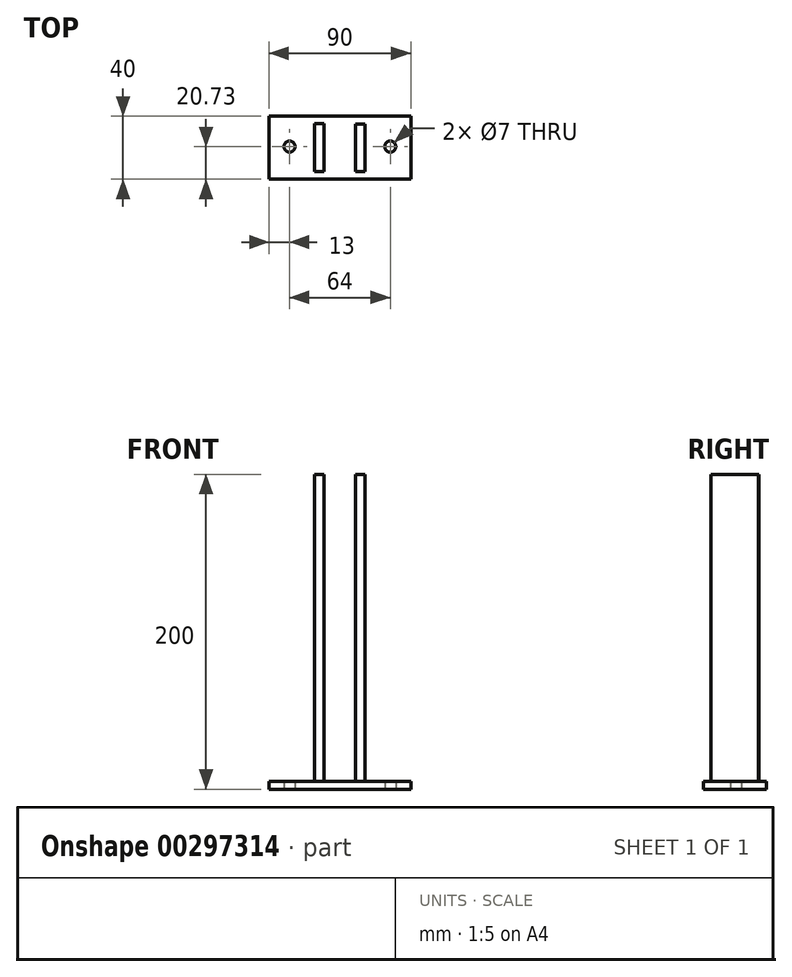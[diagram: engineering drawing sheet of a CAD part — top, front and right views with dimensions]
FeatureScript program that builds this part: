
annotation { "Feature Type Name" : "Feature", "Feature Type Description" : "" }
export const myFeature = defineFeature(function(context is Context, id is Id, definition is map)
    precondition{}
    {
        {
            var Q0;
            Q0=qCreatedBy(makeId("Right.planeOp"),FACE);
            var sketch = newSketch(context, id + "F0", { "sketchPlane" : qUnion([Q0])});
            skLineSegment(sketch, "E0.bottom", {"start": v(-20.73, 5) * mm, "end": v(19.27, 5) * mm});
            skLineSegment(sketch, "E0.left", {"start": v(-20.73, 5) * mm, "end": v(-20.73, 0) * mm});
            skLineSegment(sketch, "E0.right", {"start": v(19.27, 5) * mm, "end": v(19.27, 0) * mm});
            skLineSegment(sketch, "E1.trimOffspring", {"start": v(-20.73, 0) * mm, "end": v(19.27, 0) * mm});
            skSolve(sketch);
        }
        {
            var Q0;
            {var subQ3=sQuery(id+"F0.wireOp",EDGE,"ff7b447e-6627-4066-b775-27bb9192647b.left");Q0=makeQuery(id+"F0.imprint","IMPRINT",FACE,{"disambiguationData":[TD([[makeQuery(id+"F0.imprint","IMPRINT",EDGE,{"derivedFrom":subQ3}),-1.0]])]});}
            var Q1;
            {var subQ3=sQuery(id+"F0.wireOp",EDGE,"ff7b447e-6627-4066-b775-27bb9192647b.right");Q1=makeQuery(id+"F0.imprint","IMPRINT",FACE,{"disambiguationData":[TD([[makeQuery(id+"F0.imprint","IMPRINT",EDGE,{"derivedFrom":subQ3}),1.0]])]});}
            var Q2;
            {var subQ0=sQuery(id+"F0.wireOp",EDGE,"ff7b447e-6627-4066-b775-27bb9192647b.top");Q2=makeQuery(id+"F0.imprint","IMPRINT",FACE,{"disambiguationData":[TD([[makeQuery(id+"F0.imprint","IMPRINT",EDGE,{"derivedFrom":subQ0}),-1.0]])]});}
            var Q3;
            {var subQ5=sQuery(id+"F0.wireOp",EDGE,"E0.left");Q3=makeQuery(id+"F0.imprint","IMPRINT",FACE,{"disambiguationData":[TD([[makeQuery(id+"F0.imprint","IMPRINT",EDGE,{"derivedFrom":subQ5}),1.0]])]});}
            var Q4;
            {var subQ5=sQuery(id+"F0.wireOp",EDGE,"E0.right");Q4=makeQuery(id+"F0.imprint","IMPRINT",FACE,{"disambiguationData":[TD([[makeQuery(id+"F0.imprint","IMPRINT",EDGE,{"derivedFrom":subQ5}),-1.0]])]});}
            extrude(context, id + "F1", {"entities" : qUnion([Q0, Q1, Q2, Q3, Q4]), "depth" : 90 * mm});
        }
        {
            var Q0;
            Q0=qCreatedBy(makeId("Top.planeOp"),FACE);
            var sketch = newSketch(context, id + "F2", { "sketchPlane" : qUnion([Q0])});
            skLineSegment(sketch, "E2.bottom", {"start": v(29, 14.5) * mm, "end": v(35, 14.5) * mm});
            skLineSegment(sketch, "E2.top", {"start": v(29, -15.98) * mm, "end": v(35, -15.98) * mm});
            skLineSegment(sketch, "E2.left", {"start": v(29, 14.5) * mm, "end": v(29, -15.98) * mm});
            skLineSegment(sketch, "E2.right", {"start": v(35, 14.5) * mm, "end": v(35, -15.98) * mm});
            skLineSegment(sketch, "E3.bottom", {"start": v(55, 14.27) * mm, "end": v(61, 14.27) * mm});
            skLineSegment(sketch, "E3.top", {"start": v(55, -15.73) * mm, "end": v(61, -15.73) * mm});
            skLineSegment(sketch, "E3.left", {"start": v(55, 14.27) * mm, "end": v(55, -15.73) * mm});
            skLineSegment(sketch, "E3.right", {"start": v(61, 14.27) * mm, "end": v(61, -15.73) * mm});
            skLineSegment(sketch, "E4", {"start": v(0, -20.73) * mm, "end": v(90, -20.73) * mm, "construction": true});
            skLineSegment(sketch, "E5", {"start": v(90, 19.27) * mm, "end": v(90, -20.73) * mm, "construction": true});
            skPoint(sketch, "E6.center.orphan", {"position": v(77, 0) * mm});
            skPoint(sketch, "E7.center.orphan", {"position": v(13, 0) * mm});
            skSolve(sketch);
        }
        {
            var Q0;
            Q0 = qSketchRegion(id + "F2", true);
            extrude(context, id + "F3", {"entities" : qUnion([Q0]), "operationType" : NewBodyOperationType.ADD, "depth" : 200 * mm});
        }
        {
            var Q0;
            Q0=qCreatedBy(makeId("Top.planeOp"),FACE);
            var sketch = newSketch(context, id + "F4", { "sketchPlane" : qUnion([Q0])});
            skCircle(sketch, "E8", {"center": v(77, 0) * mm, "radius": 3.5 * mm});
            skCircle(sketch, "E9", {"center": v(13, 0) * mm, "radius": 3.5 * mm});
            skSolve(sketch);
        }
        {
            var Q0;
            Q0=sQuery(id+"F4.wireOp",VERTEX,"E9.center");
            var Q1;
            Q1=sQuery(id+"F4.wireOp",VERTEX,"E8.center");
            var Q2;
            Q2=makeQuery(id+"F1.opExtrude","SWEPT_BODY",BODY,{"disambiguationData":[OSD([sQuery(id+"F0.wireOp",EDGE,"E0.bottom"),sQuery(id+"F0.wireOp",EDGE,"E0.left"),sQuery(id+"F0.wireOp",EDGE,"E0.right"),sQuery(id+"F0.wireOp",EDGE,"E1.trimOffspring")])]});
            hole(context, id + "F5", {"style" : HoleStyle.SIMPLE, "endStyle" : HoleEndStyle.THROUGH, "oppositeDirection" : true, "holeDiameter" : 7 * mm, "tappedDepth" : 12 * mm, "tapClearance" : 3, "locations" : qUnion([Q0, Q1]), "scope" : qUnion([Q2])});
        }
    });
